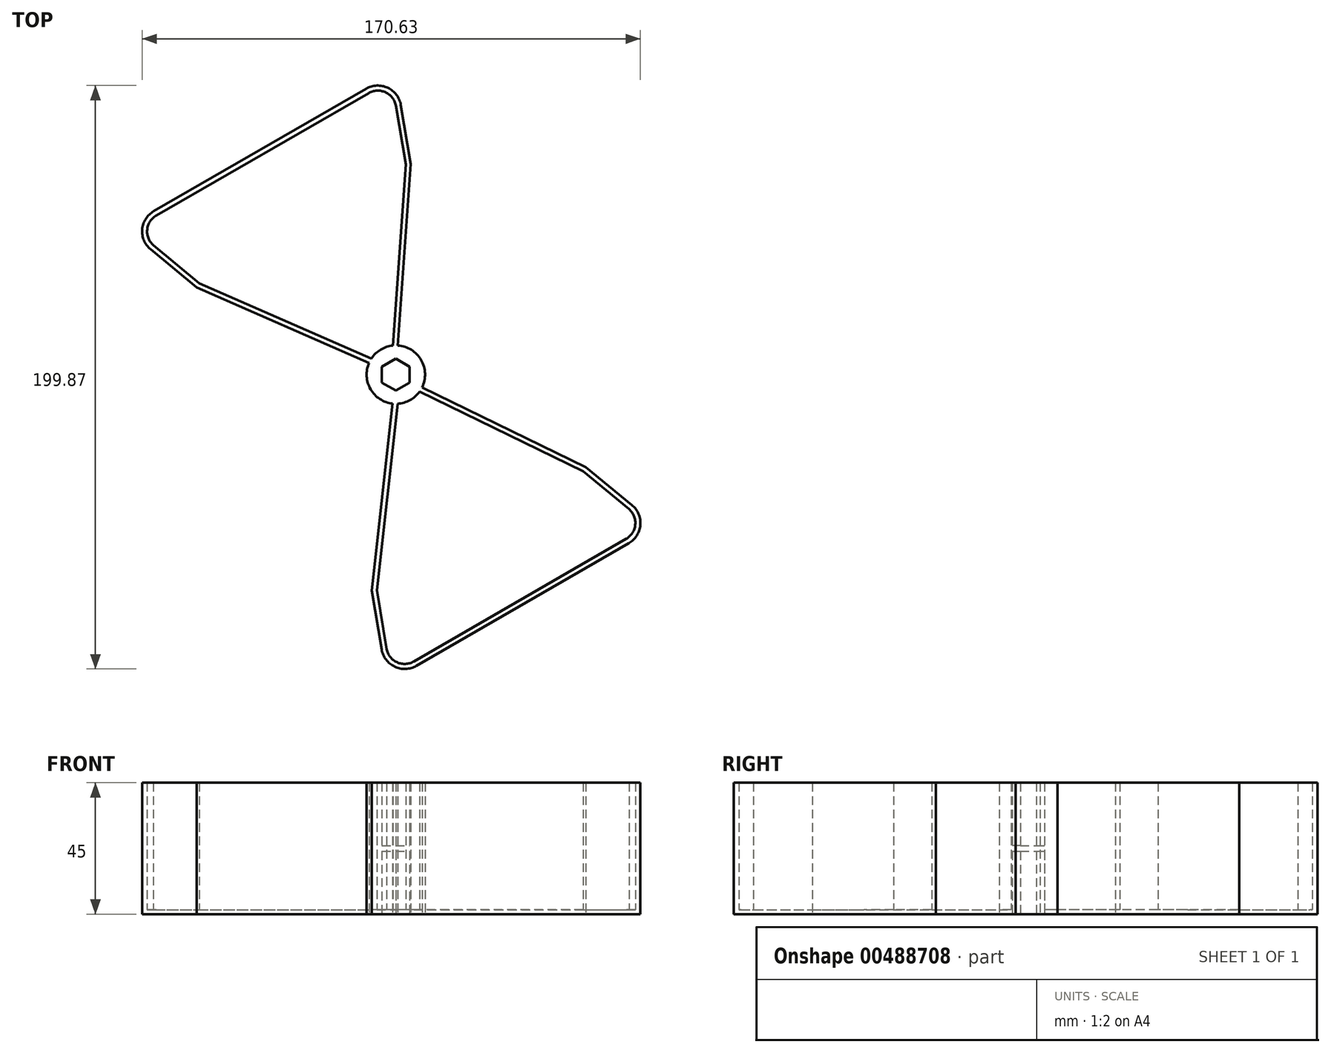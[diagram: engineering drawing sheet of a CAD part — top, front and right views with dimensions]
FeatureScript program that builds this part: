
annotation { "Feature Type Name" : "Feature", "Feature Type Description" : "" }
export const myFeature = defineFeature(function(context is Context, id is Id, definition is map)
    precondition{}
    {
        {
            var Q0;
            Q0=qCreatedBy(makeId("Top.planeOp"),FACE);
            var sketch = newSketch(context, id + "F0", { "sketchPlane" : qUnion([Q0])});
            skCircle(sketch, "E0", {"center": v(0, 0) * mm, "radius": 107 * mm});
            skLineSegment(sketch, "E1", {"start": v(92.66, 53.5) * mm, "end": v(0, 0) * mm});
            skLineSegment(sketch, "E2", {"start": v(0, 0) * mm, "end": v(-92.66, -53.5) * mm});
            skCircle(sketch, "E3", {"center": v(0, 0) * mm, "radius": 10 * mm});
            skLineSegment(sketch, "E4", {"start": v(0, 0) * mm, "end": v(-98.02, 42.92) * mm});
            skLineSegment(sketch, "E5", {"start": v(0, 0) * mm, "end": v(7.54, 106.73) * mm});
            skLineSegment(sketch, "E6", {"start": v(-82.88, 55.98) * mm, "end": v(-10.18, 97.96) * mm});
            skLineSegment(sketch, "E7", {"start": v(-83.97, 42.89) * mm, "end": v(-68.18, 29.85) * mm});
            skLineSegment(sketch, "E8", {"start": v(1.7, 92.36) * mm, "end": v(5.1, 72.16) * mm});
            skCircle(sketch, "E9.cCircle", {"center": v(0, 0) * mm, "radius": 5.5 * mm, "construction": true});
            skLineSegment(sketch, "E9.3", {"start": v(-4.76, -2.75) * mm, "end": v(-4.76, 2.75) * mm});
            skLineSegment(sketch, "E9.4", {"start": v(-4.76, 2.75) * mm, "end": v(0, 5.5) * mm});
            skLineSegment(sketch, "E9.5", {"start": v(0, 5.5) * mm, "end": v(4.76, 2.75) * mm});
            skArc(sketch, "E10.filletArc", {"start": v(-82.88, 55.98) * mm, "mid": v(-86.85, 49.72) * mm, "end": v(-83.97, 42.89) * mm});
            skArc(sketch, "E11.filletArc", {"start": v(1.7, 92.36) * mm, "mid": v(-2.77, 98.27) * mm, "end": v(-10.18, 97.96) * mm});
            skPoint(sketch, "E12", {"position": v(-46.55, 76.96) * mm});
            skLineSegment(sketch, "E13", {"start": v(-82.02, 54.52) * mm, "end": v(-9.29, 96.45) * mm});
            skLineSegment(sketch, "E14", {"start": v(-83.07, 44.35) * mm, "end": v(-67.28, 31.32) * mm});
            skLineSegment(sketch, "E15", {"start": v(-67.28, 31.32) * mm, "end": v(-3.59, 3.43) * mm});
            skLineSegment(sketch, "E16", {"start": v(3.39, 72.08) * mm, "end": v(-1.37, 4.7) * mm});
            skArc(sketch, "E17", {"start": v(-82.02, 54.52) * mm, "mid": v(-85.14, 49.7) * mm, "end": v(-83.07, 44.35) * mm});
            skLineSegment(sketch, "E18", {"start": v(3.39, 72.08) * mm, "end": v(0, 92.27) * mm});
            skArc(sketch, "E19", {"start": v(-9.29, 96.45) * mm, "mid": v(-3.58, 96.73) * mm, "end": v(0, 92.27) * mm});
            skSolve(sketch);
        }
        {
            var Q0;
            Q0=makeQuery(id+"F0.imprint","IMPRINT",FACE,{"disambiguationData":[TD([[makeQuery(id+"F0.imprint","IMPRINT",EDGE,{"derivedFrom":sQuery(id+"F0.wireOp",EDGE,"E6")}),-1.0]])]});
            var Q1;
            {var subQ0=sQuery(id+"F0.wireOp",EDGE,"E4");var subQ1=sQuery(id+"F0.wireOp",EDGE,"E3");var subQ2=makeQuery(id+"F0.imprint","INTERSECT",VERTEX,{"derivedFrom":[subQ1,subQ0]});Q1=makeQuery(id+"F0.imprint","IMPRINT",FACE,{"disambiguationData":[TD([[makeQuery(id+"F0.imprint","IMPRINT",EDGE,{"disambiguationData":[TD([[subQ2,-1.0]])],"derivedFrom":subQ1}),1.0]])]});}
            var Q2;
            {var subQ0=sQuery(id+"F0.wireOp",EDGE,"E9.5");var subQ1=sQuery(id+"F0.wireOp",EDGE,"E1");var subQ2=makeQuery(id+"F0.imprint","INTERSECT",VERTEX,{"derivedFrom":[subQ1,subQ0]});Q2=makeQuery(id+"F0.imprint","IMPRINT",FACE,{"disambiguationData":[TD([[makeQuery(id+"F0.imprint","IMPRINT",EDGE,{"disambiguationData":[TD([[subQ2,1.0]])],"derivedFrom":subQ1}),-1.0]])]});}
            var Q3;
            {var subQ0=sQuery(id+"F0.wireOp",EDGE,"E9.3");var subQ1=sQuery(id+"F0.wireOp",EDGE,"E2");var subQ2=makeQuery(id+"F0.imprint","INTERSECT",VERTEX,{"derivedFrom":[subQ1,subQ0]});Q3=makeQuery(id+"F0.imprint","IMPRINT",FACE,{"disambiguationData":[TD([[makeQuery(id+"F0.imprint","IMPRINT",EDGE,{"disambiguationData":[TD([[subQ2,-1.0]])],"derivedFrom":subQ1}),-1.0]])]});}
            var Q4;
            {var subQ0=sQuery(id+"F0.wireOp",EDGE,"AnP8olgk-p1Bm-NT7N-T9ON-dJmnkTqJIIKJ");var subQ1=sQuery(id+"F0.wireOp",EDGE,"E3");var subQ2=makeQuery(id+"F0.imprint","INTERSECT",VERTEX,{"derivedFrom":[subQ1,subQ0]});Q4=makeQuery(id+"F0.imprint","IMPRINT",FACE,{"disambiguationData":[TD([[makeQuery(id+"F0.imprint","IMPRINT",EDGE,{"disambiguationData":[TD([[subQ2,-1.0]])],"derivedFrom":subQ1}),1.0]])]});}
            var Q5;
            {var subQ0=sQuery(id+"F0.wireOp",EDGE,"E16");var subQ1=sQuery(id+"F0.wireOp",EDGE,"E3");var subQ2=makeQuery(id+"F0.imprint","INTERSECT",VERTEX,{"derivedFrom":[subQ1,subQ0]});Q5=makeQuery(id+"F0.imprint","IMPRINT",FACE,{"disambiguationData":[TD([[makeQuery(id+"F0.imprint","IMPRINT",EDGE,{"disambiguationData":[TD([[subQ2,-1.0]])],"derivedFrom":subQ1}),1.0]])]});}
            var Q6;
            {var subQ0=sQuery(id+"F0.wireOp",EDGE,"E4");var subQ1=sQuery(id+"F0.wireOp",EDGE,"E3");var subQ2=makeQuery(id+"F0.imprint","INTERSECT",VERTEX,{"derivedFrom":[subQ1,subQ0]});Q6=makeQuery(id+"F0.imprint","IMPRINT",FACE,{"disambiguationData":[TD([[makeQuery(id+"F0.imprint","IMPRINT",EDGE,{"disambiguationData":[TD([[subQ2,-1.0]])],"derivedFrom":subQ1}),1.0]])]});}
            var Q7;
            {var subQ0=sQuery(id+"F0.wireOp",EDGE,"E9.5");var subQ1=sQuery(id+"F0.wireOp",EDGE,"E1");var subQ2=makeQuery(id+"F0.imprint","INTERSECT",VERTEX,{"derivedFrom":[subQ1,subQ0]});Q7=makeQuery(id+"F0.imprint","IMPRINT",FACE,{"disambiguationData":[TD([[makeQuery(id+"F0.imprint","IMPRINT",EDGE,{"disambiguationData":[TD([[subQ2,1.0]])],"derivedFrom":subQ1}),-1.0]])]});}
            var Q8;
            {var subQ0=sQuery(id+"F0.wireOp",EDGE,"E9.3");var subQ1=sQuery(id+"F0.wireOp",EDGE,"E2");var subQ2=makeQuery(id+"F0.imprint","INTERSECT",VERTEX,{"derivedFrom":[subQ1,subQ0]});Q8=makeQuery(id+"F0.imprint","IMPRINT",FACE,{"disambiguationData":[TD([[makeQuery(id+"F0.imprint","IMPRINT",EDGE,{"disambiguationData":[TD([[subQ2,-1.0]])],"derivedFrom":subQ1}),-1.0]])]});}
            var Q9;
            {var subQ0=sQuery(id+"F0.wireOp",EDGE,"E16");var subQ1=sQuery(id+"F0.wireOp",EDGE,"E3");var subQ2=makeQuery(id+"F0.imprint","INTERSECT",VERTEX,{"derivedFrom":[subQ1,subQ0]});Q9=makeQuery(id+"F0.imprint","IMPRINT",FACE,{"disambiguationData":[TD([[makeQuery(id+"F0.imprint","IMPRINT",EDGE,{"disambiguationData":[TD([[subQ2,-1.0]])],"derivedFrom":subQ1}),1.0]])]});}
            var Q10;
            Q10=makeQuery(id+"F0.imprint","IMPRINT",FACE,{"disambiguationData":[TD([[makeQuery(id+"F0.imprint","IMPRINT",EDGE,{"derivedFrom":sQuery(id+"F0.wireOp",EDGE,"E6")}),-1.0]])]});
            var Q11;
            {var subQ2=sQuery(id+"F0.wireOp",EDGE,"E3");var subQ4=sQuery(id+"F0.wireOp",EDGE,"AnP8olgk-p1Bm-NT7N-T9ON-dJmnkTqJIIKJ");var subQ7=makeQuery(id+"F0.imprint","INTERSECT",VERTEX,{"derivedFrom":[subQ2,subQ4]});Q11=makeQuery(id+"F0.imprint","IMPRINT",FACE,{"disambiguationData":[TD([[makeQuery(id+"F0.imprint","IMPRINT",EDGE,{"disambiguationData":[TD([[subQ7,-1.0]])],"derivedFrom":subQ2}),-1.0]])]});}
            var Q12;
            {var subQ5=sQuery(id+"F0.wireOp",EDGE,"E5");var subQ6=sQuery(id+"F0.wireOp",EDGE,"E3");var subQ7=makeQuery(id+"F0.imprint","INTERSECT",VERTEX,{"derivedFrom":[subQ6,subQ5]});Q12=makeQuery(id+"F0.imprint","IMPRINT",FACE,{"disambiguationData":[TD([[makeQuery(id+"F0.imprint","IMPRINT",EDGE,{"disambiguationData":[TD([[subQ7,-1.0]])],"derivedFrom":subQ6}),1.0]])]});}
            var Q13;
            {var subQ5=sQuery(id+"F0.wireOp",EDGE,"E15");var subQ7=sQuery(id+"F0.wireOp",EDGE,"E3");var subQ8=makeQuery(id+"F0.imprint","INTERSECT",VERTEX,{"derivedFrom":[subQ7,subQ5]});Q13=makeQuery(id+"F0.imprint","IMPRINT",FACE,{"disambiguationData":[TD([[makeQuery(id+"F0.imprint","IMPRINT",EDGE,{"disambiguationData":[TD([[subQ8,-1.0]])],"derivedFrom":subQ7}),1.0]])]});}
            var Q14;
            Q14=makeQuery(id+"F0.imprint","IMPRINT",FACE,{"disambiguationData":[TD([[makeQuery(id+"F0.imprint","IMPRINT",EDGE,{"derivedFrom":sQuery(id+"F0.wireOp",EDGE,"E13")}),-1.0]])]});
            extrude(context, id + "F1", {"entities" : qUnion([Q0, Q1, Q2, Q3, Q4, Q5, Q6, Q7, Q8, Q9, Q10, Q11, Q12, Q13, Q14]), "endBound" : BoundingType.SYMMETRIC, "depth" : 45 * mm});
        }
        {
            var Q0;
            Q0=makeQuery(id+"F0.imprint","IMPRINT",FACE,{"disambiguationData":[TD([[makeQuery(id+"F0.imprint","IMPRINT",EDGE,{"derivedFrom":sQuery(id+"F0.wireOp",EDGE,"E13")}),-1.0]])]});
            extrude(context, id + "F2", {"entities" : qUnion([Q0]), "operationType" : NewBodyOperationType.REMOVE, "endBound" : BoundingType.UP_TO_NEXT, "depth" : 45 * mm});
        }
        {
            var Q0;
            Q0=makeQuery(id+"F0.imprint","IMPRINT",FACE,{"disambiguationData":[TD([[makeQuery(id+"F0.imprint","IMPRINT",EDGE,{"derivedFrom":sQuery(id+"F0.wireOp",EDGE,"E13")}),-1.0]])]});
            extrude(context, id + "F3", {"entities" : qUnion([Q0]), "operationType" : NewBodyOperationType.REMOVE, "oppositeDirection" : true, "depth" : 21 * mm});
        }
        {
            var Q0;
            {var subQ3=sQuery(id+"F0.wireOp",EDGE,"E9.4");Q0=makeQuery(id+"F0.imprint","IMPRINT",FACE,{"disambiguationData":[TD([[makeQuery(id+"F0.imprint","IMPRINT",EDGE,{"derivedFrom":subQ3}),-1.0]])]});}
            var Q1;
            {var subQ0=sQuery(id+"F0.wireOp",EDGE,"E5");var subQ3=sQuery(id+"F0.wireOp",EDGE,"E9.5");var subQ5=makeQuery(id+"F0.imprint","INTERSECT",VERTEX,{"derivedFrom":[subQ0,subQ3]});Q1=makeQuery(id+"F0.imprint","IMPRINT",FACE,{"disambiguationData":[TD([[makeQuery(id+"F0.imprint","IMPRINT",EDGE,{"disambiguationData":[TD([[subQ5,-1.0]])],"derivedFrom":subQ3}),-1.0]])]});}
            var Q2;
            {var subQ0=sQuery(id+"F0.wireOp",EDGE,"E4");var subQ3=sQuery(id+"F0.wireOp",EDGE,"E9.3");var subQ5=makeQuery(id+"F0.imprint","INTERSECT",VERTEX,{"derivedFrom":[subQ0,subQ3]});Q2=makeQuery(id+"F0.imprint","IMPRINT",FACE,{"disambiguationData":[TD([[makeQuery(id+"F0.imprint","IMPRINT",EDGE,{"disambiguationData":[TD([[subQ5,1.0]])],"derivedFrom":subQ3}),-1.0]])]});}
            var Q3;
            {var subQ0=sQuery(id+"F0.wireOp",EDGE,"E4");var subQ3=sQuery(id+"F0.wireOp",EDGE,"E9.3");var subQ5=makeQuery(id+"F0.imprint","INTERSECT",VERTEX,{"derivedFrom":[subQ0,subQ3]});Q3=makeQuery(id+"F0.imprint","IMPRINT",FACE,{"disambiguationData":[TD([[makeQuery(id+"F0.imprint","IMPRINT",EDGE,{"disambiguationData":[TD([[subQ5,-1.0]])],"derivedFrom":subQ3}),-1.0]])]});}
            var Q4;
            {var subQ0=sQuery(id+"F0.wireOp",EDGE,"E5");var subQ3=sQuery(id+"F0.wireOp",EDGE,"E9.5");var subQ5=makeQuery(id+"F0.imprint","INTERSECT",VERTEX,{"derivedFrom":[subQ0,subQ3]});Q4=makeQuery(id+"F0.imprint","IMPRINT",FACE,{"disambiguationData":[TD([[makeQuery(id+"F0.imprint","IMPRINT",EDGE,{"disambiguationData":[TD([[subQ5,1.0]])],"derivedFrom":subQ3}),-1.0]])]});}
            extrude(context, id + "F4", {"entities" : qUnion([Q0, Q1, Q2, Q3, Q4]), "operationType" : NewBodyOperationType.ADD, "endBound" : BoundingType.SYMMETRIC, "depth" : 2 * mm});
        }
        {
            var Q0;
            Q0=makeQuery(id+"F1.opExtrude","SWEPT_BODY",BODY,{"disambiguationData":[OSD([sQuery(id+"F0.wireOp",EDGE,"E1"),sQuery(id+"F0.wireOp",EDGE,"E2"),sQuery(id+"F0.wireOp",EDGE,"E3"),sQuery(id+"F0.wireOp",EDGE,"E9.3"),sQuery(id+"F0.wireOp",EDGE,"E9.4"),sQuery(id+"F0.wireOp",EDGE,"E9.5"),sQuery(id+"F0.wireOp",EDGE,"5MymaB0g-9e4g-225G-YczL-Hyq0Awh0kWlJ"),sQuery(id+"F0.wireOp",EDGE,"3N2rWDWq-xnla-HKAB-uxAZ-sxnsU2QL5Ws7"),sQuery(id+"F0.wireOp",EDGE,"obKADWan-t8Ai-73Aw-fz2r-t4hcHPqFQkrj"),sQuery(id+"F0.wireOp",EDGE,"72a574f6-7cfe-4581-9829-bbd02d96e9f3"),sQuery(id+"F0.wireOp",EDGE,"tCZ9xjj5-7H28-01Vk-cXOH-PXbSqAcNCzQk"),sQuery(id+"F0.wireOp",EDGE,"SNJ4cFE6-cJLb-4ri2-hM3X-4En6oR47e0T6"),sQuery(id+"F0.wireOp",EDGE,"dc0d57e3-8435-42b8-a426-1b19d98ab5d3")])]});
            var Q1;
            {var subQ0=sQuery(id+"F0.wireOp",EDGE,"E2");var subQ1=sQuery(id+"F0.wireOp",EDGE,"E1");Q1=makeQuery(id+"F4.boolean.opBoolean","MERGE",FACE,{"derivedFrom":[makeQuery(id+"F1.opExtrude","SWEPT_FACE",FACE,{"disambiguationData":[OSD([subQ1])]}),makeQuery(id+"F1.opExtrude","SWEPT_FACE",FACE,{"disambiguationData":[OSD([subQ0])]}),makeQuery(id+"F4.opExtrude","SWEPT_FACE",FACE,{"disambiguationData":[OSD([subQ1,subQ0])]})]});}
            mirror(context, id + "F5", {"operationType" : NewBodyOperationType.ADD, "entities" : qUnion([Q0]), "mirrorPlane" : qUnion([Q1])});
        }
    });
